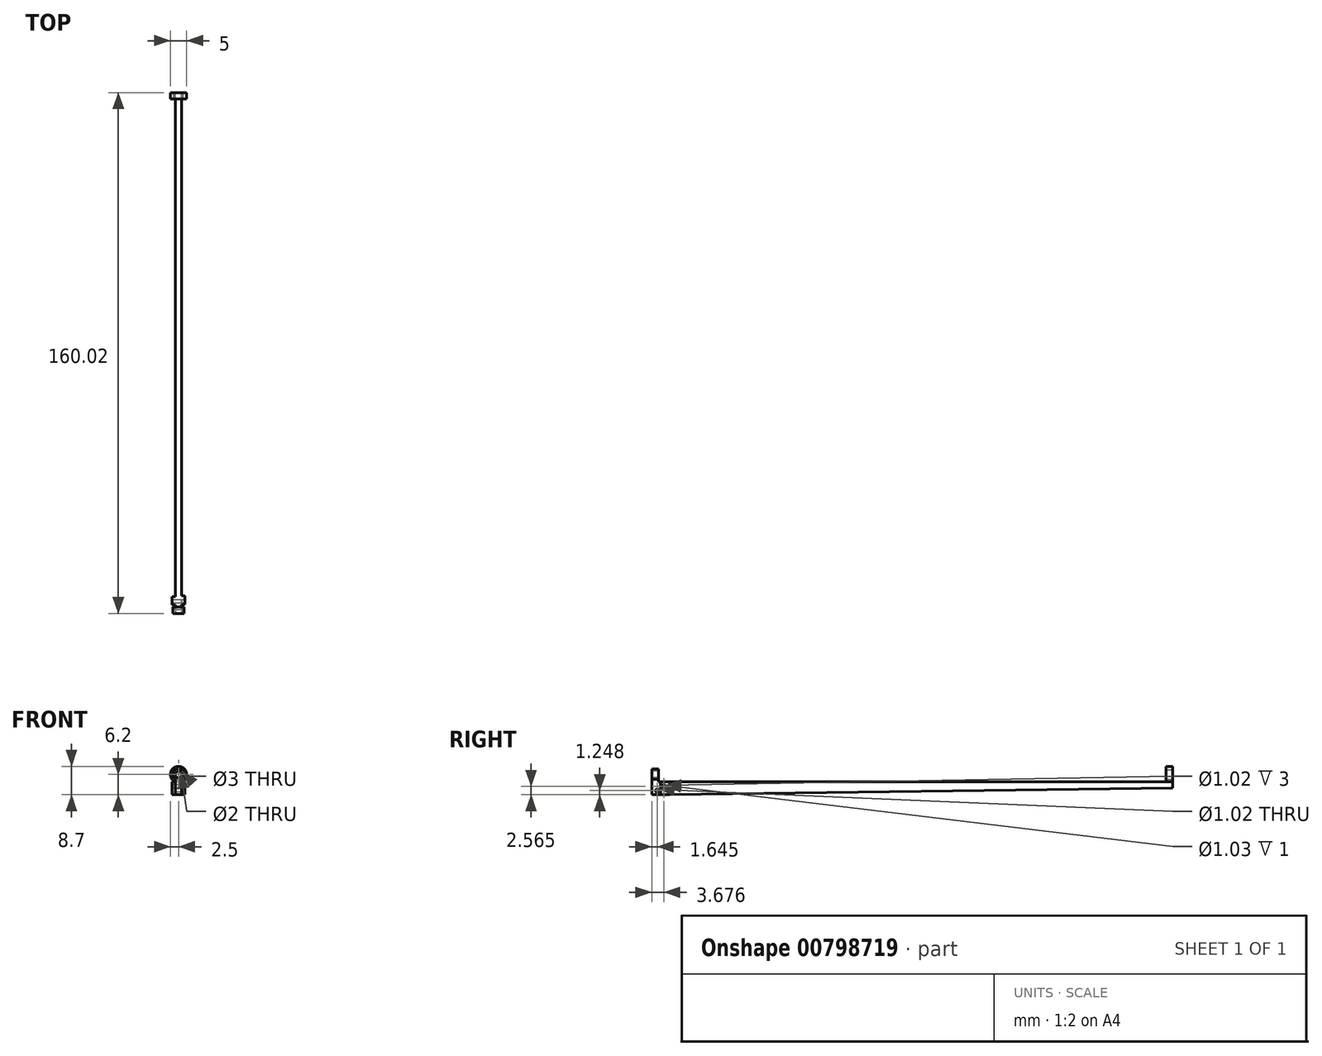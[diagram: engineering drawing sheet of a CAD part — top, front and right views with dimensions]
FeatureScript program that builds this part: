
annotation { "Feature Type Name" : "Feature", "Feature Type Description" : "" }
export const myFeature = defineFeature(function(context is Context, id is Id, definition is map)
    precondition{}
    {
        {
            var Q0;
            Q0=qCreatedBy(makeId("Right.planeOp"),FACE);
            var sketch = newSketch(context, id + "F0", { "sketchPlane" : qUnion([Q0])});
            skLineSegment(sketch, "E0", {"start": v(0, 0) * mm, "end": v(160.02, 0) * mm});
            skLineSegment(sketch, "E1", {"start": v(160.02, 0) * mm, "end": v(160.02, -2) * mm});
            skLineSegment(sketch, "E2", {"start": v(160.02, -2) * mm, "end": v(0, -4) * mm});
            skLineSegment(sketch, "E3", {"start": v(0, -4) * mm, "end": v(0, 0) * mm});
            skLineSegment(sketch, "E4", {"start": v(0, 0) * mm, "end": v(0, -2.75) * mm});
            skLineSegment(sketch, "E5", {"start": v(0, -2.75) * mm, "end": v(1.64, -2.75) * mm});
            skCircle(sketch, "E6", {"center": v(1.64, -2.75) * mm, "radius": 0.5 * mm});
            skLineSegment(sketch, "E7", {"start": v(0, 0) * mm, "end": v(3.68, 0) * mm});
            skLineSegment(sketch, "E8", {"start": v(3.68, 0) * mm, "end": v(3.68, -1.44) * mm});
            skCircle(sketch, "E9", {"center": v(3.68, -1.44) * mm, "radius": 0.5 * mm});
            skSolve(sketch);
        }
        {
            var Q0;
            Q0 = qSketchRegion(id + "F0", true);
            extrude(context, id + "F1", {"entities" : qUnion([Q0]), "depth" : 2 * mm, "offsetDistance" : 25.4 * mm});
        }
        {
            var Q0;
            Q0=makeQuery(id+"F1.opExtrude","SWEPT_FACE",FACE,{"disambiguationData":[OSD([sQuery(id+"F0.wireOp",EDGE,"E1")])]});
            var sketch = newSketch(context, id + "F2", { "sketchPlane" : qUnion([Q0])});
            skLineSegment(sketch, "E10", {"start": v(-1, 0) * mm, "end": v(-1, 2.2) * mm, "construction": true});
            skCircle(sketch, "E11", {"center": v(-1, 2.2) * mm, "radius": 1.5 * mm});
            skCircle(sketch, "E12", {"center": v(-1, 2.2) * mm, "radius": 2.5 * mm});
            skSolve(sketch);
        }
        {
            var Q0;
            Q0=makeQuery(id+"F2.imprint","IMPRINT",FACE,{"disambiguationData":[TD([[makeQuery(id+"F2.imprint","IMPRINT",EDGE,{"derivedFrom":sQuery(id+"F2.wireOp",EDGE,"E11")}),-1.0]])]});
            extrude(context, id + "F3", {"entities" : qUnion([Q0]), "operationType" : NewBodyOperationType.ADD, "oppositeDirection" : true, "depth" : 2 * mm, "offsetDistance" : 25.4 * mm});
        }
        {
            var Q0;
            Q0=makeQuery(id+"F1.opExtrude","SWEPT_FACE",FACE,{"disambiguationData":[OSD([sQuery(id+"F0.wireOp",EDGE,"E3"),sQuery(id+"F0.wireOp",EDGE,"E4")])]});
            var sketch = newSketch(context, id + "F4", { "sketchPlane" : qUnion([Q0])});
            skLineSegment(sketch, "E13", {"start": v(1, 0) * mm, "end": v(1, 2.2) * mm, "construction": true});
            skCircle(sketch, "E14", {"center": v(1, 2.2) * mm, "radius": 1 * mm});
            skArc(sketch, "E15", {"start": v(2, 0.76) * mm, "mid": v(1, 3.95) * mm, "end": v(0, 0.76) * mm});
            skLineSegment(sketch, "E16", {"start": v(0, 0) * mm, "end": v(0, 0.76) * mm});
            skLineSegment(sketch, "E17", {"start": v(2, 0) * mm, "end": v(2, 0.76) * mm});
            skSolve(sketch);
        }
        {
            var Q0;
            Q0=makeQuery(id+"F4.imprint","IMPRINT",FACE,{"disambiguationData":[TD([[makeQuery(id+"F4.imprint","IMPRINT",EDGE,{"derivedFrom":sQuery(id+"F4.wireOp",EDGE,"E14")}),-1.0]])]});
            extrude(context, id + "F5", {"entities" : qUnion([Q0]), "operationType" : NewBodyOperationType.ADD, "oppositeDirection" : true, "depth" : 2 * mm, "offsetDistance" : 25.4 * mm});
        }
        {
            var Q0;
            Q0=makeQuery(id+"F1.opExtrude","CAP_FACE",FACE,{"disambiguationData":[OSD([sQuery(id+"F0.wireOp",EDGE,"E0"),sQuery(id+"F0.wireOp",EDGE,"E1"),sQuery(id+"F0.wireOp",EDGE,"E2"),sQuery(id+"F0.wireOp",EDGE,"E3"),sQuery(id+"F0.wireOp",EDGE,"E4"),sQuery(id+"F0.wireOp",EDGE,"E6"),sQuery(id+"F0.wireOp",EDGE,"E7"),sQuery(id+"F0.wireOp",EDGE,"E9")])],"isStart":false});
            var sketch = newSketch(context, id + "F6", { "sketchPlane" : qUnion([Q0])});
            skLineSegment(sketch, "E18", {"start": v(2.75, 0) * mm, "end": v(2.75, -3.97) * mm});
            skLineSegment(sketch, "E19", {"start": v(2.75, -3.97) * mm, "end": v(5.44, -3.93) * mm});
            skLineSegment(sketch, "E20", {"start": v(5.44, -3.93) * mm, "end": v(5.44, 0) * mm});
            skLineSegment(sketch, "E21", {"start": v(5.44, 0) * mm, "end": v(2.75, 0) * mm});
            skCircle(sketch, "E22", {"center": v(3.68, -1.44) * mm, "radius": 0.51 * mm});
            skSolve(sketch);
        }
        {
            var Q0;
            Q0 = qSketchRegion(id + "F6", true);
            extrude(context, id + "F7", {"entities" : qUnion([Q0]), "operationType" : NewBodyOperationType.ADD, "depth" : 1 * mm, "offsetDistance" : 25.4 * mm});
        }
        {
            var Q0;
            Q0=makeQuery(id+"F5.boolean.opBoolean","MERGE",FACE,{"derivedFrom":[makeQuery(id+"F1.opExtrude","CAP_FACE",FACE,{"disambiguationData":[OSD([sQuery(id+"F0.wireOp",EDGE,"E0"),sQuery(id+"F0.wireOp",EDGE,"E1"),sQuery(id+"F0.wireOp",EDGE,"E2"),sQuery(id+"F0.wireOp",EDGE,"E3"),sQuery(id+"F0.wireOp",EDGE,"E4"),sQuery(id+"F0.wireOp",EDGE,"E6"),sQuery(id+"F0.wireOp",EDGE,"E7"),sQuery(id+"F0.wireOp",EDGE,"E9")])],"isStart":true}),makeQuery(id+"F5.opExtrude","SWEPT_FACE",FACE,{"disambiguationData":[OSD([sQuery(id+"F4.wireOp",EDGE,"E16")])]})]});
            var sketch = newSketch(context, id + "F8", { "sketchPlane" : qUnion([Q0])});
            skLineSegment(sketch, "E23", {"start": v(-5.19, 0) * mm, "end": v(-2.65, 0) * mm});
            skLineSegment(sketch, "E24", {"start": v(-2.65, 0) * mm, "end": v(-2.65, -3.97) * mm});
            skLineSegment(sketch, "E25", {"start": v(-2.65, -3.97) * mm, "end": v(-5.19, -3.94) * mm});
            skLineSegment(sketch, "E26", {"start": v(-5.19, -3.94) * mm, "end": v(-5.19, 0) * mm});
            skCircle(sketch, "E27", {"center": v(-3.68, -1.44) * mm, "radius": 0.5 * mm});
            skSolve(sketch);
        }
        {
            var Q0;
            Q0=makeQuery(id+"F8.imprint","IMPRINT",FACE,{"disambiguationData":[TD([[makeQuery(id+"F8.imprint","IMPRINT",EDGE,{"derivedFrom":sQuery(id+"F8.wireOp",EDGE,"E23")}),1.0]])]});
            extrude(context, id + "F9", {"entities" : qUnion([Q0]), "operationType" : NewBodyOperationType.ADD, "depth" : 1 * mm, "offsetDistance" : 25.4 * mm});
        }
    });
